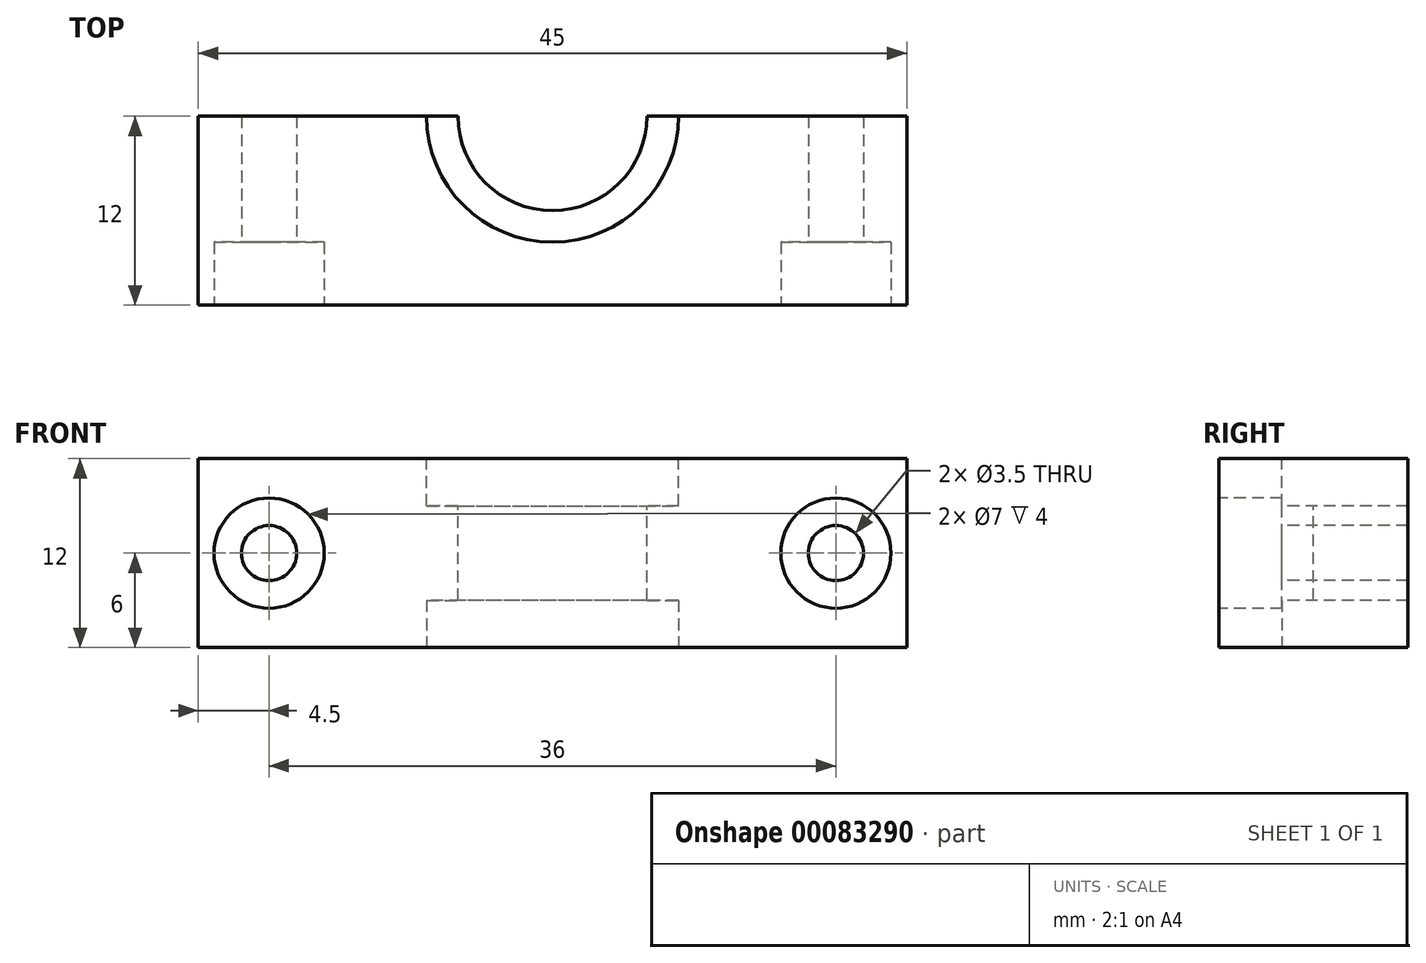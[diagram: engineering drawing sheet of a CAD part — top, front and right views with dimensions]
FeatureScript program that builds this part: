
annotation { "Feature Type Name" : "Feature", "Feature Type Description" : "" }
export const myFeature = defineFeature(function(context is Context, id is Id, definition is map)
    precondition{}
    {
        {
            var Q0;
            Q0=qCreatedBy(makeId("Front.planeOp"),FACE);
            var sketch = newSketch(context, id + "F0", { "sketchPlane" : qUnion([Q0])});
            skLineSegment(sketch, "E0.bottom", {"start": v(22.5, 6) * mm, "end": v(-22.5, 6) * mm});
            skLineSegment(sketch, "E0.top", {"start": v(22.5, -6) * mm, "end": v(-22.5, -6) * mm});
            skLineSegment(sketch, "E0.left", {"start": v(22.5, 6) * mm, "end": v(22.5, -6) * mm});
            skLineSegment(sketch, "E0.right", {"start": v(-22.5, 6) * mm, "end": v(-22.5, -6) * mm});
            skPoint(sketch, "E0.middle", {"position": v(0, 0) * mm});
            skCircle(sketch, "E1", {"center": v(-18, 0) * mm, "radius": 1.75 * mm});
            skCircle(sketch, "E2", {"center": v(-18, 0) * mm, "radius": 3.5 * mm});
            skCircle(sketch, "E3", {"center": v(18, 0) * mm, "radius": 1.75 * mm});
            skCircle(sketch, "E4", {"center": v(18, 0) * mm, "radius": 3.5 * mm});
            skSolve(sketch);
        }
        {
            var Q0;
            Q0 = qSketchRegion(id + "F0", true);
            var Q1;
            Q1=makeQuery(id+"F0.imprint","IMPRINT",FACE,{"disambiguationData":[TD([[makeQuery(id+"F0.imprint","IMPRINT",EDGE,{"derivedFrom":sQuery(id+"F0.wireOp",EDGE,"E1")}),-1.0]])]});
            var Q2;
            Q2=makeQuery(id+"F0.imprint","IMPRINT",FACE,{"disambiguationData":[TD([[makeQuery(id+"F0.imprint","IMPRINT",EDGE,{"derivedFrom":sQuery(id+"F0.wireOp",EDGE,"E3")}),-1.0]])]});
            extrude(context, id + "F1", {"entities" : qUnion([Q0, Q1, Q2]), "oppositeDirection" : true, "depth" : 12 * mm});
        }
        {
            var Q0;
            Q0=makeQuery(id+"F0.imprint","IMPRINT",FACE,{"disambiguationData":[TD([[makeQuery(id+"F0.imprint","IMPRINT",EDGE,{"derivedFrom":sQuery(id+"F0.wireOp",EDGE,"E1")}),-1.0]])]});
            var Q1;
            Q1=makeQuery(id+"F0.imprint","IMPRINT",FACE,{"disambiguationData":[TD([[makeQuery(id+"F0.imprint","IMPRINT",EDGE,{"derivedFrom":sQuery(id+"F0.wireOp",EDGE,"E3")}),-1.0]])]});
            extrude(context, id + "F2", {"entities" : qUnion([Q0, Q1]), "operationType" : NewBodyOperationType.REMOVE, "oppositeDirection" : true, "depth" : 4 * mm});
        }
        {
            var Q0;
            Q0=makeQuery(id+"F1.opExtrude","SWEPT_FACE",FACE,{"disambiguationData":[OSD([sQuery(id+"F0.wireOp",EDGE,"E0.bottom")])]});
            var sketch = newSketch(context, id + "F3", { "sketchPlane" : qUnion([Q0])});
            skCircle(sketch, "E5", {"center": v(0, 12) * mm, "radius": 6 * mm});
            skCircle(sketch, "E6", {"center": v(0, 12) * mm, "radius": 8 * mm});
            skSolve(sketch);
        }
        {
            var Q0;
            {var subQ0=sQuery(id+"F3.wireOp",EDGE,"E5");var subQ1=makeQuery(id+"F1.opExtrude","CAP_EDGE",EDGE,{"disambiguationData":[OSD([sQuery(id+"F0.wireOp",EDGE,"E0.bottom")])],"isStart":false});var subQ2=makeQuery(id+"F3.imprint","INTERSECT",VERTEX,{"disambiguationData":[OD(0.0)],"derivedFrom":[subQ1,subQ0]});Q0=makeQuery(id+"F3.imprint","IMPRINT",FACE,{"disambiguationData":[TD([[makeQuery(id+"F3.imprint","IMPRINT",EDGE,{"disambiguationData":[TD([[subQ2,-1.0]])],"derivedFrom":subQ0}),-1.0]])]});}
            var Q1;
            {var subQ0=sQuery(id+"F3.wireOp",EDGE,"E5");var subQ1=makeQuery(id+"F1.opExtrude","CAP_EDGE",EDGE,{"disambiguationData":[OSD([sQuery(id+"F0.wireOp",EDGE,"E0.bottom")])],"isStart":false});var subQ2=makeQuery(id+"F3.imprint","INTERSECT",VERTEX,{"disambiguationData":[OD(0.0)],"derivedFrom":[subQ1,subQ0]});Q1=makeQuery(id+"F3.imprint","IMPRINT",FACE,{"disambiguationData":[TD([[makeQuery(id+"F3.imprint","IMPRINT",EDGE,{"disambiguationData":[TD([[subQ2,-1.0]])],"derivedFrom":subQ0}),1.0]])]});}
            var Q2;
            {var subQ0=sQuery(id+"F3.wireOp",EDGE,"E5");var subQ1=makeQuery(id+"F1.opExtrude","CAP_EDGE",EDGE,{"disambiguationData":[OSD([sQuery(id+"F0.wireOp",EDGE,"E0.bottom")])],"isStart":false});var subQ2=makeQuery(id+"F3.imprint","INTERSECT",VERTEX,{"disambiguationData":[OD(0.0)],"derivedFrom":[subQ1,subQ0]});Q2=makeQuery(id+"F3.imprint","IMPRINT",FACE,{"disambiguationData":[TD([[makeQuery(id+"F3.imprint","IMPRINT",EDGE,{"disambiguationData":[TD([[subQ2,1.0]])],"derivedFrom":subQ0}),1.0]])]});}
            extrude(context, id + "F4", {"entities" : qUnion([Q0, Q1, Q2]), "operationType" : NewBodyOperationType.REMOVE, "endBound" : BoundingType.THROUGH_ALL, "oppositeDirection" : true, "depth" : 25 * mm});
        }
        {
            var Q0;
            Q0 = qSketchRegion(id + "F3", true);
            extrude(context, id + "F5", {"entities" : qUnion([Q0]), "operationType" : NewBodyOperationType.REMOVE, "oppositeDirection" : true, "depth" : 3 * mm});
        }
        {
            var Q0;
            Q0=makeQuery(id+"F1.opExtrude","SWEPT_FACE",FACE,{"disambiguationData":[OSD([sQuery(id+"F0.wireOp",EDGE,"E0.top")])]});
            var sketch = newSketch(context, id + "F6", { "sketchPlane" : qUnion([Q0])});
            skCircle(sketch, "E7", {"center": v(0, -12) * mm, "radius": 8 * mm});
            skSolve(sketch);
        }
        {
            var Q0;
            Q0 = qSketchRegion(id + "F6", true);
            extrude(context, id + "F7", {"entities" : qUnion([Q0]), "operationType" : NewBodyOperationType.REMOVE, "oppositeDirection" : true, "depth" : 3 * mm});
        }
    });
